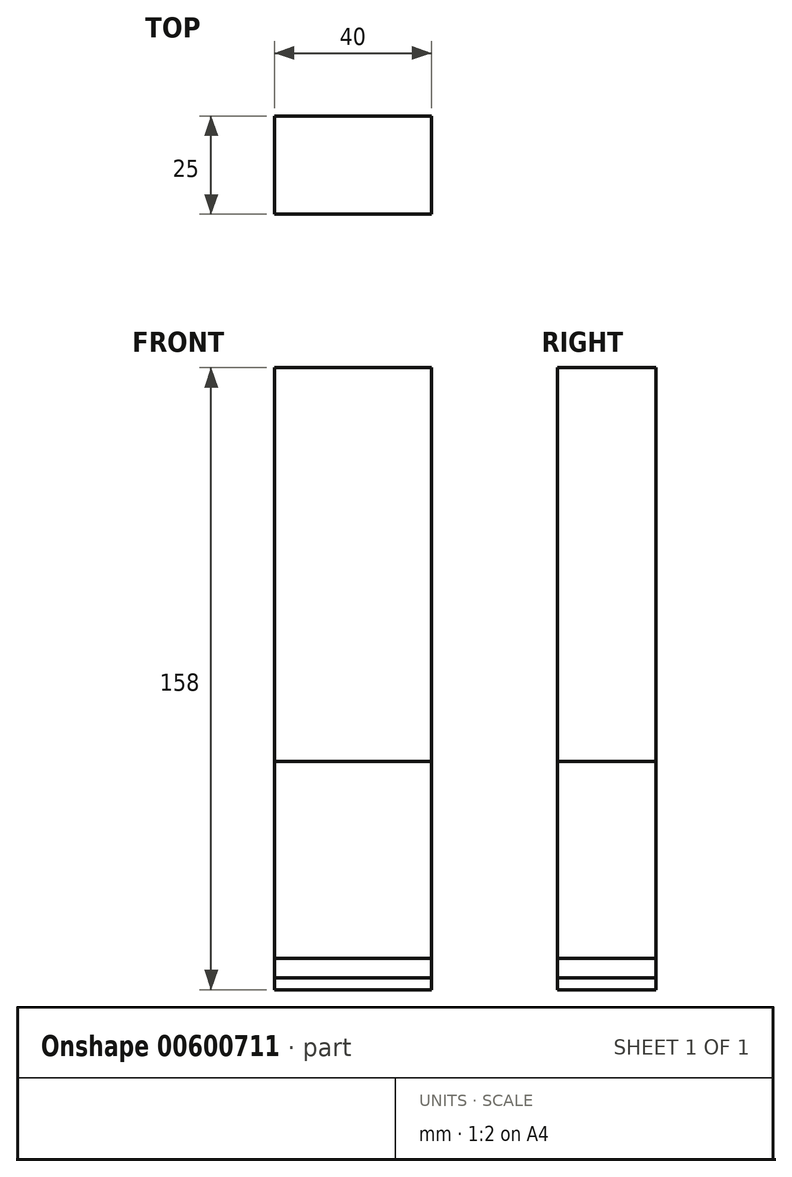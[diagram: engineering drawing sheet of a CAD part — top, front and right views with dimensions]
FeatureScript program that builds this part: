
annotation { "Feature Type Name" : "Feature", "Feature Type Description" : "" }
export const myFeature = defineFeature(function(context is Context, id is Id, definition is map)
    precondition{}
    {
        {
            var Q0;
            Q0=qCreatedBy(makeId("Front.planeOp"),FACE);
            var sketch = newSketch(context, id + "F0", { "sketchPlane" : qUnion([Q0])});
            skLineSegment(sketch, "E0", {"start": v(0, 0) * mm, "end": v(0, -20) * mm, "construction": true});
            skLineSegment(sketch, "E1", {"start": v(-20, -20) * mm, "end": v(0, -20) * mm});
            skLineSegment(sketch, "E2.MirrorCS", {"start": v(20, -20) * mm, "end": v(0, -20) * mm});
            skLineSegment(sketch, "E3", {"start": v(-20, -20) * mm, "end": v(-20, -17) * mm});
            skLineSegment(sketch, "E4", {"start": v(-20, -17) * mm, "end": v(20, -17) * mm});
            skLineSegment(sketch, "E5", {"start": v(-20, -17) * mm, "end": v(-20, -12) * mm});
            skLineSegment(sketch, "E6", {"start": v(-20, -12) * mm, "end": v(-20, 38) * mm});
            skLineSegment(sketch, "E7", {"start": v(-20, 38) * mm, "end": v(-20, 138) * mm});
            skLineSegment(sketch, "E8", {"start": v(-20, 138) * mm, "end": v(20, 138) * mm});
            skLineSegment(sketch, "E9", {"start": v(20, 138) * mm, "end": v(20, -20) * mm});
            skLineSegment(sketch, "E10", {"start": v(-20, -12) * mm, "end": v(20, -12) * mm});
            skLineSegment(sketch, "E11", {"start": v(-20, 38) * mm, "end": v(20, 38) * mm});
            skSolve(sketch);
        }
        {
            var Q0;
            Q0=makeQuery(id+"F0.imprint","IMPRINT",FACE,{"disambiguationData":[TD([[makeQuery(id+"F0.imprint","IMPRINT",EDGE,{"derivedFrom":sQuery(id+"F0.wireOp",EDGE,"E7")}),-1.0]])]});
            extrude(context, id + "F1", {"entities" : qUnion([Q0]), "depth" : 25 * mm, "offsetDistance" : 25 * mm});
        }
        {
            var Q0;
            Q0=makeQuery(id+"F0.imprint","IMPRINT",FACE,{"disambiguationData":[TD([[makeQuery(id+"F0.imprint","IMPRINT",EDGE,{"derivedFrom":sQuery(id+"F0.wireOp",EDGE,"E6")}),-1.0]])]});
            extrude(context, id + "F2", {"entities" : qUnion([Q0]), "depth" : 25 * mm, "offsetDistance" : 25 * mm});
        }
        {
            var Q0;
            {var subQ0=sQuery(id+"F0.wireOp",EDGE,"E4");Q0=makeQuery(id+"F0.imprint","IMPRINT",FACE,{"disambiguationData":[TD([[makeQuery(id+"F0.imprint","IMPRINT",EDGE,{"derivedFrom":subQ0}),1.0]])]});}
            extrude(context, id + "F3", {"entities" : qUnion([Q0]), "depth" : 25 * mm, "offsetDistance" : 25 * mm});
        }
        {
            var Q0;
            Q0=makeQuery(id+"F0.imprint","IMPRINT",FACE,{"disambiguationData":[TD([[makeQuery(id+"F0.imprint","IMPRINT",EDGE,{"derivedFrom":sQuery(id+"F0.wireOp",EDGE,"E1")}),1.0]])]});
            extrude(context, id + "F4", {"entities" : qUnion([Q0]), "depth" : 25 * mm, "offsetDistance" : 25 * mm});
        }
    });
